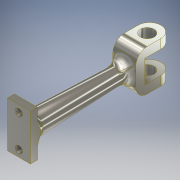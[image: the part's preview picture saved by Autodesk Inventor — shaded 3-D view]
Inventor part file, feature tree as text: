
AUTODESK INVENTOR PART (.ipt)
format: ipt  version: 2017 (Build 210142000, 142)  size: 307,712 bytes
history: native  units: mm
features: sketch x8, extrude x6, fillet x3, plane x1, loft x1
ambient origin geometry x8: Origin, YZ Plane, XZ Plane, XY Plane, X Axis, Y Axis, Z Axis, Center Point
bodies: Solid1 (feature_tree)
feature tree (19):
  sketch  "Sketch1"  dims[d0=9.5mm d1=43.0mm d2=6.5mm]
  plane  "Work Plane1"
  loft  "Loft1"
  extrude  "Extrusion1"  TaperAngle=0.0deg  [1 undecoded]
  extrude  "Extrusion2"  Depth=3.0mm TaperAngle=0.0deg
  extrude  "Extrusion3"  Depth=3.0mm
  fillet  "Fillet1"  [1 undecoded]
  extrude  "Extrusion5"  Depth=9.5mm
  extrude  "Extrusion6"  TaperAngle=0.0deg  [1 undecoded]
  extrude  "Extrusion7"  TaperAngle=0.0deg  [1 undecoded]
  fillet  "Fillet3"  [1 undecoded]
  fillet  "Fillet4"  [1 undecoded]
  sketch  "Sketch2"  dims[d3=0.0mm d4=90.0deg d5=0.0mm d6=90.0deg]
  sketch  "Sketch3"  dims[d7=5.0mm d8=10.0mm d9=10.0mm d10=20.0mm d11=10.0mm d12=3.0mm d13=0.0mm]
  sketch  "Sketch4"  dims[d14=10.0mm d15=3.0mm d16=0.0mm]
  sketch  "Sketch5"  dims[d17=3.0mm d18=14.0mm d19=3.0mm d20=3.0mm d21=5.0mm d22=0.0mm d29=3.0mm d31=0.0mm]
  sketch  "Sketch7"  dims[d32=0.0mm d33=9.5mm]
  sketch  "Sketch8"  dims[d34=5.0mm d35=0.0mm]
  sketch  "Sketch9"  dims[d36=5.0mm d37=0.0mm d38=0.0mm d39=0.0mm d40=10.0mm d41=5.0mm d42=0.0mm d43=10.0mm d54=5.0mm d55=10.0mm d56=9.0mm d57=18.0mm d58=10.0mm d59=10.0mm d60=18.0mm d61=4.0mm d62=0.0mm d64=4.0mm d65=12.0mm d66=0.0mm d67=6.0mm d68=12.0mm d69=0.0mm d70=5.0mm d71=5.0mm d72=14.0mm d73=53.0mm]
note: 6 required parameter values undecoded (feature->parameter linkage not recoverable at this tier; creation-order binding heuristic only, values carry confidence <= 0.55)
